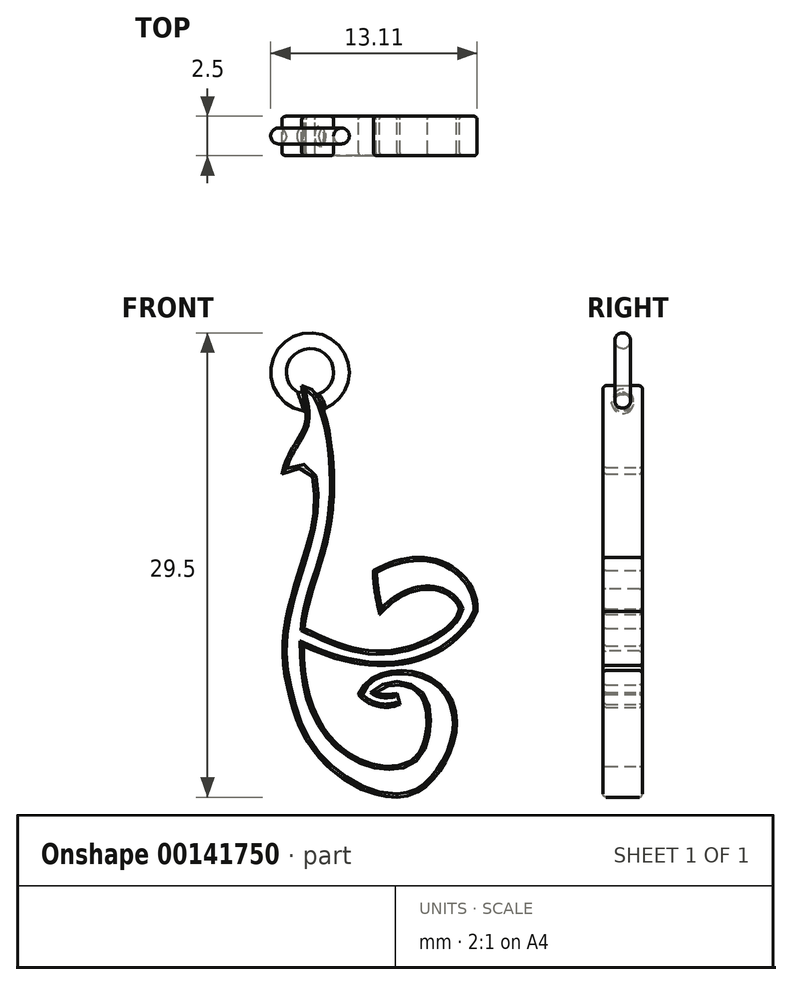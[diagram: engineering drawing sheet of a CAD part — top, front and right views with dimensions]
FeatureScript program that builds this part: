
annotation { "Feature Type Name" : "Feature", "Feature Type Description" : "" }
export const myFeature = defineFeature(function(context is Context, id is Id, definition is map)
    precondition{}
    {
        {
            var Q0;
            Q0=qCreatedBy(makeId("Front.planeOp"),FACE);
            var sketch = newSketch(context, id + "F0", { "sketchPlane" : qUnion([Q0])});
            skLineSegment(sketch, "E0.bottom", {"start": v(0, 0) * mm, "end": v(12.5, 0) * mm, "construction": true});
            skLineSegment(sketch, "E0.top", {"start": v(0, 25.5) * mm, "end": v(12.5, 25.5) * mm, "construction": true});
            skLineSegment(sketch, "E0.left", {"start": v(0, 0) * mm, "end": v(0, 25.5) * mm, "construction": true});
            skLineSegment(sketch, "E0.right", {"start": v(12.5, 0) * mm, "end": v(12.5, 25.5) * mm, "construction": true});
            skFitSpline(sketch, "E1", {"points": [v(-1.79, 20.54) * mm, v(-0.92, 20.82) * mm, v(-0.33, 20.94) * mm, v(0, 20.78) * mm, v(0.29, 19.6) * mm, v(0.17, 17.5) * mm, v(-0.46, 15.1) * mm, v(-1.68, 10.2) * mm, v(-1.3, 6.43) * mm, v(0.37, 2.78) * mm, v(5.53, 0) * mm], "startDerivative": vector(20.38, 8.6) * mm, "endDerivative": vector(38.03, 0) * mm});
            skFitSpline(sketch, "E2", {"points": [v(5.53, 0) * mm, v(7.96, 1.29) * mm, v(9.3, 4.47) * mm, v(8.42, 7.01) * mm, v(5.96, 8.04) * mm, v(3.78, 7.47) * mm, v(3.07, 6.52) * mm], "startDerivative": vector(18.23, 0.98) * mm, "endDerivative": vector(-5, -7.89) * mm});
            skFitSpline(sketch, "E3", {"points": [v(3.07, 6.52) * mm, v(5.72, 5.9) * mm], "startDerivative": vector(1.9, -2.36) * mm, "endDerivative": vector(2.57, 1.21) * mm});
            skLineSegment(sketch, "E4", {"start": v(5.72, 5.9) * mm, "end": v(5.53, 6.58) * mm});
            skFitSpline(sketch, "E5", {"points": [v(5.53, 6.58) * mm, v(4.18, 6.67) * mm], "startDerivative": vector(-1.3, -0.15) * mm, "endDerivative": vector(-1.11, 0.69) * mm});
            skFitSpline(sketch, "E6", {"points": [v(4.18, 6.67) * mm, v(5.5, 7.14) * mm, v(6.83, 6.7) * mm, v(7.45, 4.84) * mm, v(6.74, 2.55) * mm, v(5.26, 1.97) * mm, v(3.37, 2.3) * mm, v(1.2, 3.93) * mm, v(-0.18, 6.98) * mm, v(-0.42, 9.62) * mm, v(-0.37, 10.72) * mm, v(-0.07, 12.37) * mm, v(1.17, 16.67) * mm, v(1.5, 19.82) * mm, v(1.3, 22.58) * mm, v(-0.52, 26.14) * mm], "startDerivative": vector(32.08, 23.67) * mm, "endDerivative": vector(-39.2, -1.63) * mm});
            skFitSpline(sketch, "E7", {"points": [v(-0.37, 10.72) * mm, v(4.94, 9.3) * mm, v(9.5, 11.97) * mm], "startDerivative": vector(10.72, -4.83) * mm, "endDerivative": vector(2.03, 8.43) * mm});
            skFitSpline(sketch, "E8", {"points": [v(9.5, 11.97) * mm, v(4.43, 11.6) * mm], "startDerivative": vector(-1.73, 4.47) * mm, "endDerivative": vector(-6, -6.96) * mm});
            skFitSpline(sketch, "E9", {"points": [v(4.43, 11.6) * mm, v(4.03, 14.4) * mm], "startDerivative": vector(-0.68, 3.18) * mm, "endDerivative": vector(0, 3.02) * mm});
            skFitSpline(sketch, "E10", {"points": [v(-0.42, 9.62) * mm, v(10.6, 11.78) * mm], "startDerivative": vector(19.42, -9.21) * mm, "endDerivative": vector(2.4, 5.95) * mm});
            skFitSpline(sketch, "E11", {"points": [v(4.03, 14.4) * mm, v(10.6, 11.78) * mm], "startDerivative": vector(12.69, 6.95) * mm, "endDerivative": vector(-0.7, -5.73) * mm});
            skCircle(sketch, "E12", {"center": v(-0.02, 25.48) * mm, "radius": 0.4 * mm, "construction": true});
            skFitSpline(sketch, "E13", {"points": [v(-0.52, 26.14) * mm, v(-0.3, 23.78) * mm, v(-1.21, 22) * mm, v(-1.79, 20.54) * mm], "startDerivative": vector(1.01, -8.44) * mm, "endDerivative": vector(-1.4, -5.31) * mm});
            skSolve(sketch);
        }
        {
            var Q0;
            {var subQ0=sQuery(id+"F0.wireOp",EDGE,"E7");Q0=makeQuery(id+"F0.imprint","IMPRINT",FACE,{"disambiguationData":[TD([[makeQuery(id+"F0.imprint","IMPRINT",EDGE,{"derivedFrom":subQ0}),-1.0]])]});}
            var Q1;
            Q1=makeQuery(id+"F0.imprint","IMPRINT",FACE,{"disambiguationData":[TD([[makeQuery(id+"F0.imprint","IMPRINT",EDGE,{"derivedFrom":sQuery(id+"F0.wireOp",EDGE,"E1")}),1.0]])]});
            extrude(context, id + "F1", {"entities" : qUnion([Q0, Q1]), "depth" : 1.25 * mm, "offsetDistance" : 25 * mm, "hasSecondDirection" : true, "secondDirectionOppositeDirection" : true, "secondDirectionDepth" : 1.25 * mm});
        }
        {
            var Q0;
            Q0=makeQuery(id+"F1.opExtrude","CAP_EDGE",EDGE,{"disambiguationData":[OSD([sQuery(id+"F0.wireOp",EDGE,"4681fdc7-3070-4394-86cc-40bf6d9edfaf")])],"isStart":false});
            var Q1;
            Q1=makeQuery(id+"F1.opExtrude","CAP_FACE",FACE,{"disambiguationData":[OSD([sQuery(id+"F0.wireOp",EDGE,"4681fdc7-3070-4394-86cc-40bf6d9edfaf"),sQuery(id+"F0.wireOp",EDGE,"E1"),sQuery(id+"F0.wireOp",EDGE,"E2"),sQuery(id+"F0.wireOp",EDGE,"E3"),sQuery(id+"F0.wireOp",EDGE,"E4"),sQuery(id+"F0.wireOp",EDGE,"E5"),sQuery(id+"F0.wireOp",EDGE,"E6"),sQuery(id+"F0.wireOp",EDGE,"E7"),sQuery(id+"F0.wireOp",EDGE,"E8"),sQuery(id+"F0.wireOp",EDGE,"E9"),sQuery(id+"F0.wireOp",EDGE,"E10"),sQuery(id+"F0.wireOp",EDGE,"E11")])],"isStart":false});
            var Q2;
            Q2=makeQuery(id+"F1.opExtrude","CAP_FACE",FACE,{"disambiguationData":[OSD([sQuery(id+"F0.wireOp",EDGE,"4681fdc7-3070-4394-86cc-40bf6d9edfaf"),sQuery(id+"F0.wireOp",EDGE,"E1"),sQuery(id+"F0.wireOp",EDGE,"E2"),sQuery(id+"F0.wireOp",EDGE,"E3"),sQuery(id+"F0.wireOp",EDGE,"E4"),sQuery(id+"F0.wireOp",EDGE,"E5"),sQuery(id+"F0.wireOp",EDGE,"E6"),sQuery(id+"F0.wireOp",EDGE,"E7"),sQuery(id+"F0.wireOp",EDGE,"E8"),sQuery(id+"F0.wireOp",EDGE,"E9"),sQuery(id+"F0.wireOp",EDGE,"E10"),sQuery(id+"F0.wireOp",EDGE,"E11")])],"isStart":true});
            fillet(context, id + "F2", {"entities" : qUnion([Q0, Q1, Q2]), "tangentPropagation" : true, "radius" : 0.2 * mm, "defaultsChanged" : false, "vertexSettings" : [], "allowEdgeOverflow" : false});
        }
        {
            var Q0;
            Q0=qCreatedBy(makeId("Right.planeOp"),FACE);
            var sketch = newSketch(context, id + "F3", { "sketchPlane" : qUnion([Q0])});
            skCircle(sketch, "E14", {"center": v(0, 25) * mm, "radius": 0.5 * mm});
            skLineSegment(sketch, "E15", {"start": v(-3.3, 27) * mm, "end": v(3.34, 27) * mm, "construction": true});
            skSolve(sketch);
        }
        {
            var Q0;
            Q0 = qSketchRegion(id + "F3", true);
            var Q1;
            Q1=sQuery(id+"F3.wireOp",EDGE,"E15");
            revolve(context, id + "F4", {"operationType" : NewBodyOperationType.ADD, "surfaceOperationType" : NewSurfaceOperationType.NEW, "entities" : qUnion([Q0]), "axis" : qUnion([Q1]), "revolveType" : RevolveType.FULL});
        }
        {
            var Q0;
            {var subQ0=sQuery(id+"F0.wireOp",EDGE,"E6");Q0=makeQuery(id+"F4.boolean.opBoolean","INTERSECT",EDGE,{"derivedFrom":[makeQuery(id+"F1.opExtrude","SWEPT_FACE",FACE,{"disambiguationData":[OSD([subQ0]),TDD([makeQuery(id+"F0.imprint","IMPRINT",EDGE,{"disambiguationData":[TD([[makeQuery(id+"F0.imprint","INTERSECT",VERTEX,{"derivedFrom":[subQ0,sQuery(id+"F0.wireOp",EDGE,"E13")]}),1.0]])],"derivedFrom":subQ0})])]}),makeQuery(id+"F4.opRevolve","SWEPT_FACE",FACE,{"disambiguationData":[OSD([sQuery(id+"F3.wireOp",EDGE,"E14")])]})]});}
            var Q1;
            Q1=makeQuery(id+"F4.boolean.opBoolean","INTERSECT",EDGE,{"derivedFrom":[makeQuery(id+"F1.opExtrude","SWEPT_FACE",FACE,{"disambiguationData":[OSD([sQuery(id+"F0.wireOp",EDGE,"E13")])]}),makeQuery(id+"F4.opRevolve","SWEPT_FACE",FACE,{"disambiguationData":[OSD([sQuery(id+"F3.wireOp",EDGE,"E14")])]})]});
            fillet(context, id + "F5", {"entities" : qUnion([Q0, Q1]), "tangentPropagation" : true, "radius" : 0.2 * mm, "defaultsChanged" : true, "vertexSettings" : [], "allowEdgeOverflow" : false});
        }
    });
